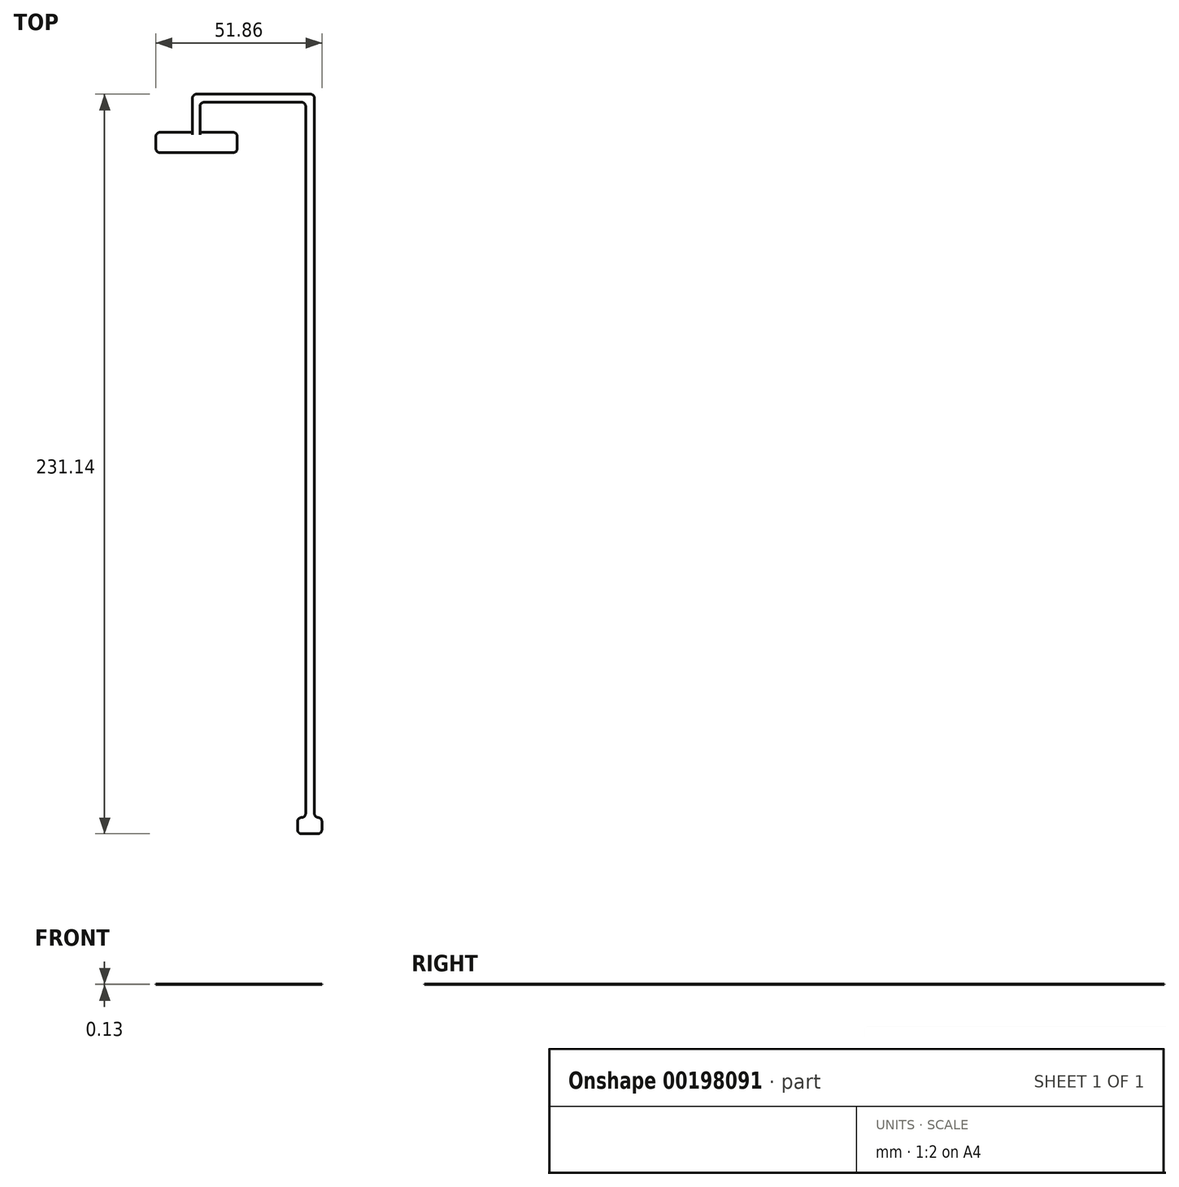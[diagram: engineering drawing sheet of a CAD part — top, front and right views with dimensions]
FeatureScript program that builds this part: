
annotation { "Feature Type Name" : "Feature", "Feature Type Description" : "" }
export const myFeature = defineFeature(function(context is Context, id is Id, definition is map)
    precondition{}
    {
        {
            var Q0;
            Q0=qCreatedBy(makeId("Top.planeOp"),FACE);
            var sketch = newSketch(context, id + "F0", { "sketchPlane" : qUnion([Q0])});
            skLineSegment(sketch, "E0.bottom", {"start": v(1.27, 0) * mm, "end": v(24.13, 0) * mm});
            skLineSegment(sketch, "E0.top", {"start": v(1.27, 6.35) * mm, "end": v(11.4, 6.35) * mm});
            skLineSegment(sketch, "E0.left", {"start": v(0, 1.27) * mm, "end": v(0, 5.08) * mm});
            skLineSegment(sketch, "E0.right", {"start": v(25.4, 1.27) * mm, "end": v(25.4, 5.08) * mm});
            skLineSegment(sketch, "E1.left", {"start": v(13.76, 14.48) * mm, "end": v(13.76, 5.59) * mm});
            skLineSegment(sketch, "E1.right", {"start": v(11.43, 17.02) * mm, "end": v(11.43, 5.59) * mm});
            skLineSegment(sketch, "E2", {"start": v(11.43, 5.59) * mm, "end": v(11.4, 5.59) * mm});
            skLineSegment(sketch, "E3", {"start": v(11.4, 5.59) * mm, "end": v(11.4, 6.35) * mm});
            skLineSegment(sketch, "E4.trimOffspring", {"start": v(13.78, 6.35) * mm, "end": v(24.13, 6.35) * mm});
            skLineSegment(sketch, "E5", {"start": v(13.78, 5.59) * mm, "end": v(13.78, 6.35) * mm});
            skLineSegment(sketch, "E6", {"start": v(13.76, 5.59) * mm, "end": v(13.78, 5.59) * mm});
            skLineSegment(sketch, "E7", {"start": v(12.7, 18.29) * mm, "end": v(48.26, 18.29) * mm});
            skLineSegment(sketch, "E8", {"start": v(15.03, 15.75) * mm, "end": v(45.5, 15.75) * mm});
            skLineSegment(sketch, "E9", {"start": v(46.78, 14.48) * mm, "end": v(46.78, -206.5) * mm});
            skLineSegment(sketch, "E10", {"start": v(49.53, 17.02) * mm, "end": v(49.53, -206.5) * mm});
            skLineSegment(sketch, "E11", {"start": v(44.24, -211.58) * mm, "end": v(44.24, -209.04) * mm});
            skLineSegment(sketch, "E12", {"start": v(45.5, -207.77) * mm, "end": v(45.5, -207.77) * mm});
            skLineSegment(sketch, "E13", {"start": v(51.86, -209.04) * mm, "end": v(51.86, -211.58) * mm});
            skPoint(sketch, "E14.visualSharp", {"position": v(0, 6.35) * mm});
            skArc(sketch, "E14.filletArc", {"start": v(1.27, 6.35) * mm, "mid": v(0.37, 5.98) * mm, "end": v(0, 5.08) * mm});
            skPoint(sketch, "E15.visualSharp", {"position": v(0, 0) * mm});
            skArc(sketch, "E15.filletArc", {"start": v(0, 1.27) * mm, "mid": v(0.37, 0.37) * mm, "end": v(1.27, 0) * mm});
            skPoint(sketch, "E16.visualSharp", {"position": v(25.4, 6.35) * mm});
            skArc(sketch, "E16.filletArc", {"start": v(25.4, 5.08) * mm, "mid": v(25.03, 5.98) * mm, "end": v(24.13, 6.35) * mm});
            skPoint(sketch, "E17.visualSharp", {"position": v(25.4, 0) * mm});
            skArc(sketch, "E17.filletArc", {"start": v(24.13, 0) * mm, "mid": v(25.03, 0.37) * mm, "end": v(25.4, 1.27) * mm});
            skPoint(sketch, "E18.visualSharp", {"position": v(11.43, 18.29) * mm});
            skArc(sketch, "E18.filletArc", {"start": v(12.7, 18.29) * mm, "mid": v(11.8, 17.92) * mm, "end": v(11.43, 17.02) * mm});
            skPoint(sketch, "E19.visualSharp", {"position": v(13.76, 15.75) * mm});
            skArc(sketch, "E19.filletArc", {"start": v(15.03, 15.75) * mm, "mid": v(14.13, 15.38) * mm, "end": v(13.76, 14.48) * mm});
            skPoint(sketch, "E20.visualSharp", {"position": v(46.78, 15.75) * mm});
            skArc(sketch, "E20.filletArc", {"start": v(46.78, 14.48) * mm, "mid": v(46.4, 15.38) * mm, "end": v(45.5, 15.75) * mm});
            skPoint(sketch, "E21.visualSharp", {"position": v(49.53, 18.29) * mm});
            skArc(sketch, "E21.filletArc", {"start": v(49.53, 17.02) * mm, "mid": v(49.16, 17.92) * mm, "end": v(48.26, 18.29) * mm});
            skPoint(sketch, "E22.visualSharp", {"position": v(46.78, -207.77) * mm});
            skArc(sketch, "E22.filletArc", {"start": v(45.5, -207.77) * mm, "mid": v(46.4, -207.4) * mm, "end": v(46.78, -206.5) * mm});
            skPoint(sketch, "E23.visualSharp", {"position": v(44.24, -207.77) * mm});
            skArc(sketch, "E23.filletArc", {"start": v(45.5, -207.77) * mm, "mid": v(44.6, -208.14) * mm, "end": v(44.24, -209.04) * mm});
            skPoint(sketch, "E24.visualSharp", {"position": v(44.24, -212.85) * mm});
            skArc(sketch, "E24.filletArc", {"start": v(44.24, -211.58) * mm, "mid": v(44.62, -212.49) * mm, "end": v(45.53, -212.85) * mm});
            skPoint(sketch, "E25.visualSharp", {"position": v(51.86, -207.86) * mm});
            skPoint(sketch, "E26.visualSharp", {"position": v(51.86, -212.84) * mm});
            skArc(sketch, "E26.filletArc", {"start": v(50.61, -212.85) * mm, "mid": v(51.5, -212.47) * mm, "end": v(51.86, -211.58) * mm});
            skPoint(sketch, "E27.visualSharp", {"position": v(49.53, -207.77) * mm});
            skArc(sketch, "E27.filletArc", {"start": v(49.53, -206.5) * mm, "mid": v(49.86, -207.36) * mm, "end": v(50.68, -207.77) * mm});
            skLineSegment(sketch, "E28", {"start": v(45.53, -212.85) * mm, "end": v(50.61, -212.85) * mm});
            skLineSegment(sketch, "E29", {"start": v(50.68, -207.77) * mm, "end": v(50.7, -207.77) * mm});
            skLineSegment(sketch, "E30", {"start": v(51.86, -209.03) * mm, "end": v(51.86, -209.04) * mm});
            skArc(sketch, "E31.filletArc", {"start": v(51.86, -209.03) * mm, "mid": v(51.52, -208.17) * mm, "end": v(50.7, -207.77) * mm});
            skSolve(sketch);
        }
        {
            var Q0;
            Q0 = qSketchRegion(id + "F0", true);
            extrude(context, id + "F1", {"entities" : qUnion([Q0]), "depth" : 0.13 * mm});
        }
    });
